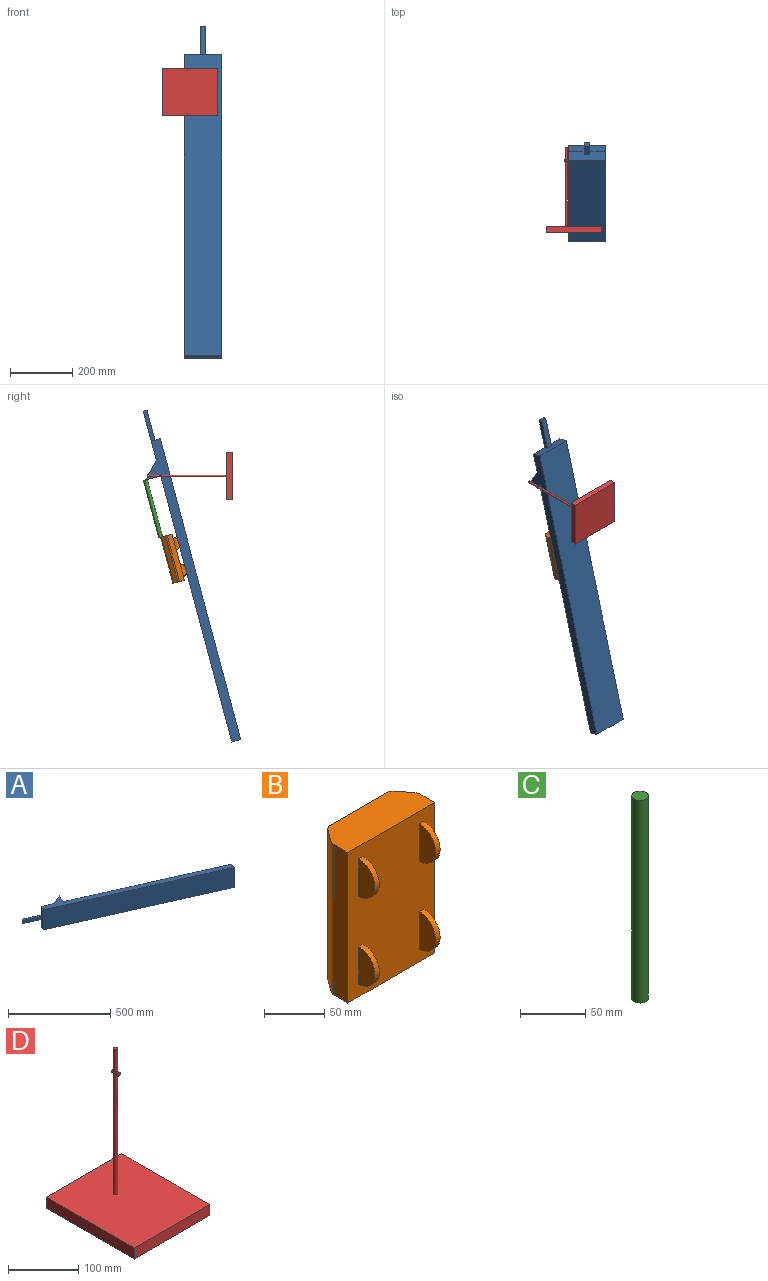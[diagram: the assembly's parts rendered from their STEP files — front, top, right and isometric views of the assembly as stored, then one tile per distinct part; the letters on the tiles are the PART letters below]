
ASSEMBLY  parts=4 mates=3
PART A: 13 faces, bbox 1010.2x474.6x120 mm
  f0: plane 807.76x359.39mm, normal (0.41,0.91,0), area 106092mm2, adj f5,f7,f8,f11
  f1: plane 91.37x40.65mm, normal (-0.41,-0.91,0), area 1840mm2, adj f2,f3,f9,f10
  f2: plane 18.4x11.6mm, normal (-0.91,0.41,0), area 233.7mm2, adj f1,f6,f9,f10
  f3: plane 120x27.41mm, normal (-0.91,0.41,0), area 3366.3mm2, adj f1,f4,f6,f7,f8,f9,f10
  f4: plane 913.65x406.5mm, normal (-0.41,-0.91,0), area 120000mm2, adj f3,f5,f7,f8
  f5: plane 120x27.41mm, normal (0.91,-0.41,0), area 3600mm2, adj f0,f4,f7,f8
  f6: plane 150.84x120mm, normal (0.41,0.91,0), area 9652mm2, adj f2,f3,f7,f8,f9,f10,f12
  f7: plane 925.85x433.91mm, normal (0,0,1), area 31290.3mm2, adj f0,f3,f4,f5,f6,f11,f12
  f8: plane 925.85x433.91mm, normal (0,0,-1), area 31290.3mm2, adj f0,f3,f4,f5,f6,f11,f12
  f9: plane 96.53x52.25mm, normal (0,0,1), area 1270mm2, adj f1,f2,f3,f6
  f10: plane 96.53x52.25mm, normal (0,0,-1), area 1270mm2, adj f1,f2,f3,f6
  f11: plane 120x46.41mm, normal (0.91,-0.41,0), area 6096mm2, adj f0,f7,f8,f12
  f12: plane 120x67.06mm, normal (-0.36,0.93,0), area 8621mm2, adj f6,f7,f8,f11
PART B: 24 faces, bbox 101.6x57.2x152.4 mm
  f0: plane 152.4x101.6mm, normal (0,-1,0), area 14709.6mm2, adj f1,f5,f6,f7,f12,f13,f14,f15
  f1: plane 152.4x16.14mm, normal (1,0,0), area 2459.7mm2, adj f0,f6,f7,f10
  f2: plane 152.4x13.07mm, normal (0.81,0.59,0), area 2470.1mm2, adj f6,f7,f10,f11
  f3: plane 152.4x64.65mm, normal (0,1,0), area 9852.7mm2, adj f6,f7,f8,f11
  f4: plane 152.4x13.07mm, normal (-0.81,0.59,0), area 2470.1mm2, adj f6,f7,f8,f9
  f5: plane 152.4x16.14mm, normal (-1,0,0), area 2459.7mm2, adj f0,f6,f7,f9
  f6: plane 101.6x38.1mm, normal (0,0,1), area 3597.1mm2, adj f0,f1,f2,f3,f4,f5,f8,f9
  f7: plane 101.6x38.1mm, normal (0,0,-1), area 3597.1mm2, adj f0,f1,f2,f3,f4,f5,f8,f9
  f8: cylinder r=8.89mm len=152.4mm, axis (0,0,-1), area 1270.9mm2, adj f3,f4,f6,f7
  f9: cylinder r=8.89mm len=152.4mm, axis (0,0,-1), area 857.3mm2, adj f4,f5,f6,f7
  f10: cylinder r=8.89mm len=152.4mm, axis (0,0,-1), area 857.3mm2, adj f1,f2,f6,f7
  f11: cylinder r=8.89mm len=152.4mm, axis (0,0,-1), area 1270.9mm2, adj f2,f3,f6,f7
  f12: cylinder r=19.05mm len=38.1mm, axis (-1,0,0), area 304mm2, adj f0,f13,f14
  f13: plane 38.1x19.05mm, normal (-1,0,0), area 570mm2, adj f0,f12
  f14: plane 38.1x19.05mm, normal (1,0,0), area 570mm2, adj f0,f12
  f15: cylinder r=19.05mm len=38.1mm, axis (-1,0,0), area 304mm2, adj f0,f16,f17
  f16: plane 38.1x19.05mm, normal (-1,0,0), area 570mm2, adj f0,f15
  f17: plane 38.1x19.05mm, normal (1,0,0), area 570mm2, adj f0,f15
  f18: plane 38.1x19.05mm, normal (-1,0,0), area 570mm2, adj f0,f19
  f19: cylinder r=19.05mm len=38.1mm, axis (-1,0,0), area 304mm2, adj f0,f18,f20
  f20: plane 38.1x19.05mm, normal (1,0,0), area 570mm2, adj f0,f19
  f21: plane 38.1x19.05mm, normal (-1,0,0), area 570mm2, adj f0,f22
  f22: cylinder r=19.05mm len=38.1mm, axis (-1,0,0), area 304mm2, adj f0,f21,f23
  f23: plane 38.1x19.05mm, normal (1,0,0), area 570mm2, adj f0,f22
PART C: 3 faces, bbox 12.7x12.7x190.5 mm
  f0: cylinder r=6.35mm len=190.5mm, axis (0,0,-1), area 7600.6mm2, adj f1,f2
  f1: plane 12.7x12.7mm, normal (0,0,1), area 126.7mm2, adj f0
  f2: plane 12.7x12.7mm, normal (0,0,-1), area 126.7mm2, adj f0
PART D: 11 faces, bbox 152.4x177.8x273.1 mm
  f0: cylinder r=3.17mm len=11.18mm, axis (0,1,0), area 143.1mm2, adj f1,f9,f10
  f1: cylinder r=3.17mm len=254mm, axis (0,0,-1), area 4987.2mm2, adj f0,f5,f8
  f2: plane 177.8x19.05mm, normal (-1,0,0), area 3387.1mm2, adj f3,f5,f6,f7
  f3: plane 177.8x152.4mm, normal (0,0,-1), area 27096.7mm2, adj f2,f4,f6,f7
  f4: plane 177.8x19.05mm, normal (1,0,0), area 3387.1mm2, adj f3,f5,f6,f7
  f5: plane 177.8x152.4mm, normal (0,0,1), area 27065.1mm2, adj f1,f2,f4,f6,f7
  f6: plane 152.4x19.05mm, normal (0,-1,0), area 2903.2mm2, adj f2,f3,f4,f5
  f7: plane 152.4x19.05mm, normal (0,1,0), area 2903.2mm2, adj f2,f3,f4,f5
  f8: plane 6.35x6.35mm, normal (0,0,1), area 31.7mm2, adj f1
  f9: plane 6.35x6.35mm, normal (0,-1,0), area 31.7mm2, adj f0
  f10: plane 6.35x6.35mm, normal (0,1,0), area 31.7mm2, adj f0
PLACE A rot(axis=(0.08,0.99,0.08),90.4deg) t=(-107.95,-105.43,-409.31)mm
PLACE B rot(axis=(0,-0.99,0.13),180deg) t=(-47.95,184.4,-187.72)mm
PLACE C rot(axis=(1,0,0),165deg) t=(-47.95,270.43,-13.53)mm
PLACE D rot(axis=(-0.58,0.58,0.58),120deg) t=(-177.8,-9.53,76.2)mm
MATE fastened C.f0 <-> A.f11  axis (0,0.26,0.97) through (-47.95,270.43,-13.53)mm
MATE fastened C.f0 <-> B.f7  axis (0,-0.26,-0.97) through (-47.95,221.21,-197.56)mm
MATE revolute D.f0 <-> A.f8  axis (1,0,0) through (-107.95,221.36,-0.4)mm
